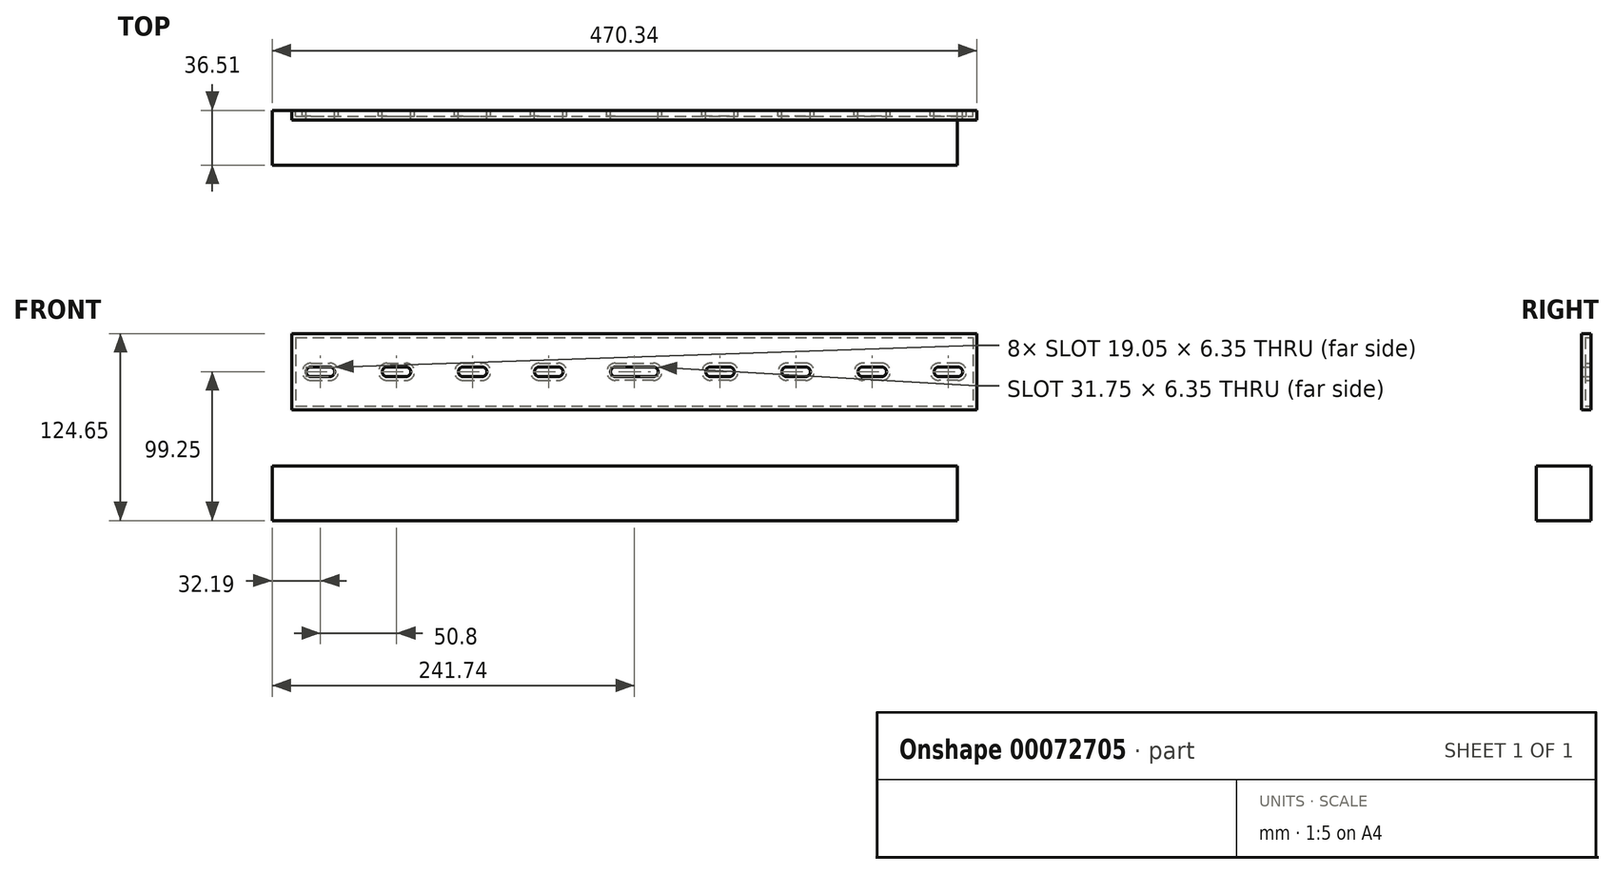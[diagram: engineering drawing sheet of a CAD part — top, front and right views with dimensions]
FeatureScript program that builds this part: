
annotation { "Feature Type Name" : "Feature", "Feature Type Description" : "" }
export const myFeature = defineFeature(function(context is Context, id is Id, definition is map)
    precondition{}
    {
        {
            var Q0;
            Q0=qCreatedBy(makeId("Front.planeOp"),FACE);
            var sketch = newSketch(context, id + "F0", { "sketchPlane" : qUnion([Q0])});
            skLineSegment(sketch, "E0.bottom", {"start": v(-457.2, 50.8) * mm, "end": v(0, 50.8) * mm});
            skLineSegment(sketch, "E0.top", {"start": v(-457.2, 0) * mm, "end": v(0, 0) * mm});
            skLineSegment(sketch, "E0.left", {"start": v(-457.2, 50.8) * mm, "end": v(-457.2, 0) * mm});
            skLineSegment(sketch, "E0.right", {"start": v(0, 50.8) * mm, "end": v(0, 0) * mm});
            skLineSegment(sketch, "E1", {"start": v(-228.6, 50.8) * mm, "end": v(-228.6, 0) * mm, "construction": true});
            skCircle(sketch, "E2", {"center": v(-228.6, 25.4) * mm, "radius": 3.17 * mm});
            skCircle(sketch, "E3", {"center": v(-241.3, 25.4) * mm, "radius": 3.17 * mm});
            skLineSegment(sketch, "E4", {"start": v(-241.3, 28.57) * mm, "end": v(-228.6, 28.57) * mm});
            skLineSegment(sketch, "E5", {"start": v(-241.3, 22.22) * mm, "end": v(-228.6, 22.22) * mm});
            skLineSegment(sketch, "E6.MirrorCS", {"start": v(-215.9, 28.57) * mm, "end": v(-228.6, 28.57) * mm});
            skLineSegment(sketch, "E7.MirrorCS", {"start": v(-215.9, 22.22) * mm, "end": v(-228.6, 22.22) * mm});
            skCircle(sketch, "E8.MirrorC", {"center": v(-215.9, 25.4) * mm, "radius": 3.17 * mm});
            skCircle(sketch, "E9.1.0.0", {"center": v(-279.4, 25.4) * mm, "radius": 3.17 * mm});
            skLineSegment(sketch, "E9.1.0.1", {"start": v(-292.1, 28.57) * mm, "end": v(-279.4, 28.57) * mm});
            skLineSegment(sketch, "E9.1.0.2", {"start": v(-292.1, 22.22) * mm, "end": v(-279.4, 22.22) * mm});
            skCircle(sketch, "E9.1.0.3", {"center": v(-292.1, 25.4) * mm, "radius": 3.17 * mm});
            skCircle(sketch, "E9.2.0.0", {"center": v(-330.2, 25.4) * mm, "radius": 3.17 * mm});
            skLineSegment(sketch, "E9.2.0.1", {"start": v(-342.9, 28.57) * mm, "end": v(-330.2, 28.57) * mm});
            skLineSegment(sketch, "E9.2.0.2", {"start": v(-342.9, 22.22) * mm, "end": v(-330.2, 22.22) * mm});
            skCircle(sketch, "E9.2.0.3", {"center": v(-342.9, 25.4) * mm, "radius": 3.17 * mm});
            skCircle(sketch, "E9.3.0.0", {"center": v(-381, 25.4) * mm, "radius": 3.17 * mm});
            skLineSegment(sketch, "E9.3.0.1", {"start": v(-393.7, 28.57) * mm, "end": v(-381, 28.57) * mm});
            skLineSegment(sketch, "E9.3.0.2", {"start": v(-393.7, 22.22) * mm, "end": v(-381, 22.22) * mm});
            skCircle(sketch, "E9.3.0.3", {"center": v(-393.7, 25.4) * mm, "radius": 3.17 * mm});
            skCircle(sketch, "E9.4.0.0", {"center": v(-431.8, 25.4) * mm, "radius": 3.17 * mm});
            skLineSegment(sketch, "E9.4.0.1", {"start": v(-444.5, 28.57) * mm, "end": v(-431.8, 28.57) * mm});
            skLineSegment(sketch, "E9.4.0.2", {"start": v(-444.5, 22.22) * mm, "end": v(-431.8, 22.22) * mm});
            skCircle(sketch, "E9.4.0.3", {"center": v(-444.5, 25.4) * mm, "radius": 3.17 * mm});
            skLineSegment(sketch, "E9.direction1", {"start": v(-228.6, 25.4) * mm, "end": v(-279.4, 25.4) * mm, "construction": true});
            skCircle(sketch, "E10.MirrorC", {"center": v(-25.4, 25.4) * mm, "radius": 3.17 * mm});
            skCircle(sketch, "E11.MirrorC", {"center": v(-177.8, 25.4) * mm, "radius": 3.17 * mm});
            skCircle(sketch, "E12.MirrorC", {"center": v(-114.3, 25.4) * mm, "radius": 3.17 * mm});
            skCircle(sketch, "E13.MirrorC", {"center": v(-127, 25.4) * mm, "radius": 3.17 * mm});
            skCircle(sketch, "E14.MirrorC", {"center": v(-76.2, 25.4) * mm, "radius": 3.17 * mm});
            skCircle(sketch, "E15.MirrorC", {"center": v(-63.5, 25.4) * mm, "radius": 3.17 * mm});
            skCircle(sketch, "E16.MirrorC", {"center": v(-12.7, 25.4) * mm, "radius": 3.17 * mm});
            skCircle(sketch, "E17.MirrorC", {"center": v(-165.1, 25.4) * mm, "radius": 3.17 * mm});
            skLineSegment(sketch, "E18.MirrorCS", {"start": v(-114.3, 22.22) * mm, "end": v(-127, 22.22) * mm});
            skLineSegment(sketch, "E19.MirrorCS", {"start": v(-63.5, 22.22) * mm, "end": v(-76.2, 22.22) * mm});
            skLineSegment(sketch, "E20.MirrorCS", {"start": v(-12.7, 28.57) * mm, "end": v(-25.4, 28.57) * mm});
            skLineSegment(sketch, "E21.MirrorCS", {"start": v(-114.3, 28.57) * mm, "end": v(-127, 28.57) * mm});
            skLineSegment(sketch, "E22.MirrorCS", {"start": v(-63.5, 28.57) * mm, "end": v(-76.2, 28.57) * mm});
            skLineSegment(sketch, "E23.MirrorCS", {"start": v(-165.1, 28.57) * mm, "end": v(-177.8, 28.57) * mm});
            skLineSegment(sketch, "E24.MirrorCS", {"start": v(-165.1, 22.22) * mm, "end": v(-177.8, 22.22) * mm});
            skLineSegment(sketch, "E25.MirrorCS", {"start": v(-12.7, 22.22) * mm, "end": v(-25.4, 22.22) * mm});
            skSolve(sketch);
        }
        {
            var Q0;
            Q0=makeQuery(id+"F0.imprint","IMPRINT",FACE,{"disambiguationData":[TD([[makeQuery(id+"F0.imprint","IMPRINT",EDGE,{"derivedFrom":sQuery(id+"F0.wireOp",EDGE,"E0.bottom")}),-1.0]])]});
            extrude(context, id + "F1", {"entities" : qUnion([Q0]), "depth" : 6.35 * mm});
        }
        {
            var Q0;
            Q0=makeQuery(id+"F1.opExtrude","CAP_FACE",FACE,{"disambiguationData":[OSD([sQuery(id+"F0.wireOp",EDGE,"E0.bottom"),sQuery(id+"F0.wireOp",EDGE,"E0.top"),sQuery(id+"F0.wireOp",EDGE,"E0.left"),sQuery(id+"F0.wireOp",EDGE,"E0.right"),sQuery(id+"F0.wireOp",EDGE,"E3"),sQuery(id+"F0.wireOp",EDGE,"E4"),sQuery(id+"F0.wireOp",EDGE,"E5"),sQuery(id+"F0.wireOp",EDGE,"E6.MirrorCS"),sQuery(id+"F0.wireOp",EDGE,"E7.MirrorCS"),sQuery(id+"F0.wireOp",EDGE,"E8.MirrorC"),sQuery(id+"F0.wireOp",EDGE,"E9.1.0.0"),sQuery(id+"F0.wireOp",EDGE,"E9.1.0.1"),sQuery(id+"F0.wireOp",EDGE,"E9.1.0.2"),sQuery(id+"F0.wireOp",EDGE,"E9.1.0.3"),sQuery(id+"F0.wireOp",EDGE,"E9.2.0.0"),sQuery(id+"F0.wireOp",EDGE,"E9.2.0.1"),sQuery(id+"F0.wireOp",EDGE,"E9.2.0.2"),sQuery(id+"F0.wireOp",EDGE,"E9.2.0.3"),sQuery(id+"F0.wireOp",EDGE,"E9.3.0.0"),sQuery(id+"F0.wireOp",EDGE,"E9.3.0.1"),sQuery(id+"F0.wireOp",EDGE,"E9.3.0.2"),sQuery(id+"F0.wireOp",EDGE,"E9.3.0.3"),sQuery(id+"F0.wireOp",EDGE,"E9.4.0.0"),sQuery(id+"F0.wireOp",EDGE,"E9.4.0.1"),sQuery(id+"F0.wireOp",EDGE,"E9.4.0.2"),sQuery(id+"F0.wireOp",EDGE,"E9.4.0.3"),sQuery(id+"F0.wireOp",EDGE,"E10.MirrorC"),sQuery(id+"F0.wireOp",EDGE,"E11.MirrorC"),sQuery(id+"F0.wireOp",EDGE,"E12.MirrorC"),sQuery(id+"F0.wireOp",EDGE,"E13.MirrorC"),sQuery(id+"F0.wireOp",EDGE,"E14.MirrorC"),sQuery(id+"F0.wireOp",EDGE,"E15.MirrorC"),sQuery(id+"F0.wireOp",EDGE,"E16.MirrorC"),sQuery(id+"F0.wireOp",EDGE,"E17.MirrorC"),sQuery(id+"F0.wireOp",EDGE,"E18.MirrorCS"),sQuery(id+"F0.wireOp",EDGE,"E19.MirrorCS"),sQuery(id+"F0.wireOp",EDGE,"E20.MirrorCS"),sQuery(id+"F0.wireOp",EDGE,"E21.MirrorCS"),sQuery(id+"F0.wireOp",EDGE,"E22.MirrorCS"),sQuery(id+"F0.wireOp",EDGE,"E23.MirrorCS"),sQuery(id+"F0.wireOp",EDGE,"E24.MirrorCS"),sQuery(id+"F0.wireOp",EDGE,"E25.MirrorCS")])],"isStart":true});
            shell(context, id + "F2", {"entities" : qUnion([Q0]), "thickness" : 2.54 * mm});
        }
        {
            var Q0;
            Q0=qCreatedBy(makeId("Front.planeOp"),FACE);
            var sketch = newSketch(context, id + "F3", { "sketchPlane" : qUnion([Q0])});
            skLineSegment(sketch, "E26.bottom", {"start": v(-13.14, -37.34) * mm, "end": v(-470.34, -37.34) * mm});
            skLineSegment(sketch, "E26.top", {"start": v(-13.14, -73.85) * mm, "end": v(-470.34, -73.85) * mm});
            skLineSegment(sketch, "E26.left", {"start": v(-13.14, -37.34) * mm, "end": v(-13.14, -73.85) * mm});
            skLineSegment(sketch, "E26.right", {"start": v(-470.34, -37.34) * mm, "end": v(-470.34, -73.85) * mm});
            skSolve(sketch);
        }
        {
            var Q0;
            Q0=makeQuery(id+"F3.imprint","IMPRINT",FACE,{"disambiguationData":[TD([[makeQuery(id+"F3.imprint","IMPRINT",EDGE,{"derivedFrom":sQuery(id+"F3.wireOp",EDGE,"E26.bottom")}),1.0]])]});
            extrude(context, id + "F4", {"entities" : qUnion([Q0]), "depth" : 36.5 * mm});
        }
    });
